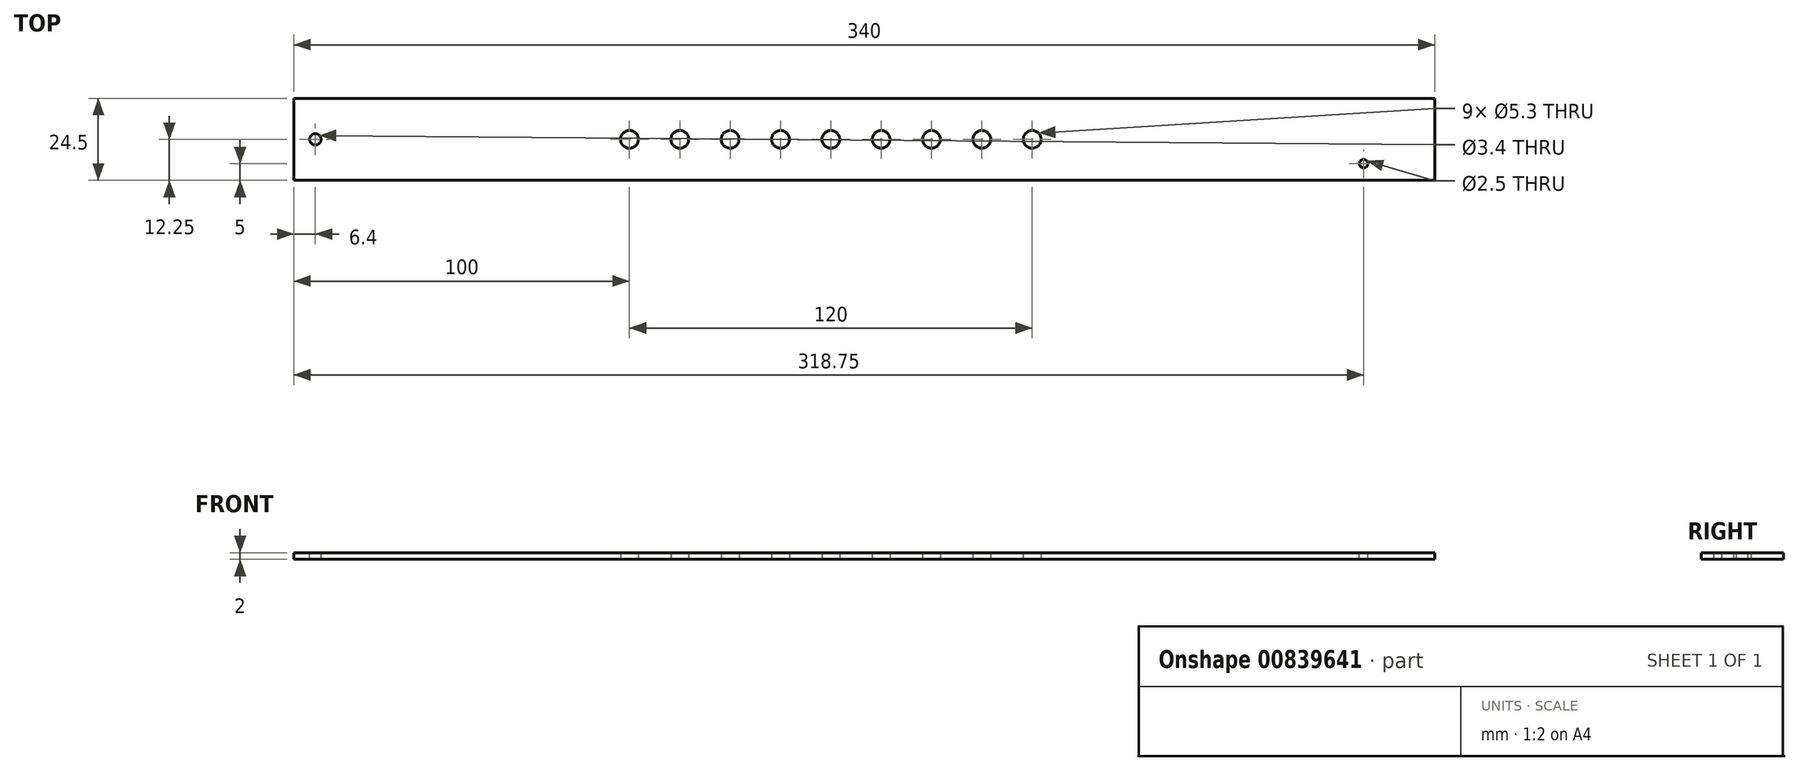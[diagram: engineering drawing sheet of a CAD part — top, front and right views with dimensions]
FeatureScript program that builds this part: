
annotation { "Feature Type Name" : "Feature", "Feature Type Description" : "" }
export const myFeature = defineFeature(function(context is Context, id is Id, definition is map)
    precondition{}
    {
        {
            var Q0;
            Q0=qCreatedBy(makeId("Top.planeOp"),FACE);
            var sketch = newSketch(context, id + "F0", { "sketchPlane" : qUnion([Q0])});
            skLineSegment(sketch, "E0.bottom", {"start": v(150, -12.25) * mm, "end": v(-150, -12.25) * mm});
            skLineSegment(sketch, "E0.top", {"start": v(150, 12.25) * mm, "end": v(-150, 12.25) * mm});
            skLineSegment(sketch, "E0.left", {"start": v(150, -12.25) * mm, "end": v(150, 12.25) * mm});
            skLineSegment(sketch, "E0.right", {"start": v(-150, -12.25) * mm, "end": v(-150, 12.25) * mm});
            skPoint(sketch, "E0.middle", {"position": v(0, 0) * mm});
            skCircle(sketch, "E1.5.0.0", {"center": v(-60, 0) * mm, "radius": 2.65 * mm});
            skCircle(sketch, "E1.6.0.0", {"center": v(-45, 0) * mm, "radius": 2.65 * mm});
            skCircle(sketch, "E1.7.0.0", {"center": v(-30, 0) * mm, "radius": 2.65 * mm});
            skCircle(sketch, "E1.8.0.0", {"center": v(-15, 0) * mm, "radius": 2.65 * mm});
            skCircle(sketch, "E1.9.0.0", {"center": v(0, 0) * mm, "radius": 2.65 * mm});
            skCircle(sketch, "E1.10.0.0", {"center": v(15, 0) * mm, "radius": 2.65 * mm});
            skCircle(sketch, "E1.11.0.0", {"center": v(30, 0) * mm, "radius": 2.65 * mm});
            skCircle(sketch, "E1.12.0.0", {"center": v(45, 0) * mm, "radius": 2.65 * mm});
            skCircle(sketch, "E1.13.0.0", {"center": v(60, 0) * mm, "radius": 2.65 * mm});
            skLineSegment(sketch, "E1.direction1", {"start": v(-135, 0) * mm, "end": v(-120, 0) * mm, "construction": true});
            skSolve(sketch);
        }
        {
            var Q0;
            Q0=makeQuery(id+"F0.imprint","IMPRINT",FACE,{"disambiguationData":[TD([[makeQuery(id+"F0.imprint","IMPRINT",EDGE,{"derivedFrom":sQuery(id+"F0.wireOp",EDGE,"E0.bottom")}),-1.0]])]});
            extrude(context, id + "F1", {"entities" : qUnion([Q0]), "depth" : 2 * mm, "offsetDistance" : 25 * mm});
        }
        {
            var Q0;
            Q0=makeQuery(id+"F1.opExtrude","SWEPT_FACE",FACE,{"disambiguationData":[OSD([sQuery(id+"F0.wireOp",EDGE,"E0.right")])]});
            extrude(context, id + "F2", {"entities" : qUnion([Q0]), "operationType" : NewBodyOperationType.ADD, "depth" : 10 * mm, "offsetDistance" : 25 * mm});
        }
        {
            var Q0;
            Q0=makeQuery(id+"F1.opExtrude","SWEPT_FACE",FACE,{"disambiguationData":[OSD([sQuery(id+"F0.wireOp",EDGE,"E0.left")])]});
            extrude(context, id + "F3", {"entities" : qUnion([Q0]), "operationType" : NewBodyOperationType.ADD, "depth" : 30 * mm, "offsetDistance" : 25 * mm});
        }
        {
            var Q0;
            {var subQ0=sQuery(id+"F0.wireOp",EDGE,"E0.left");var subQ1=sQuery(id+"F0.wireOp",EDGE,"E0.right");Q0=makeQuery(id+"F3.boolean.opBoolean","MERGE",FACE,{"derivedFrom":[makeQuery(id+"F2.boolean.opBoolean","MERGE",FACE,{"derivedFrom":[makeQuery(id+"F1.opExtrude","CAP_FACE",FACE,{"disambiguationData":[OSD([sQuery(id+"F0.wireOp",EDGE,"E0.bottom"),sQuery(id+"F0.wireOp",EDGE,"E0.top"),subQ0,subQ1,sQuery(id+"F0.wireOp",EDGE,"LckrCdrf-Oz9b-iWqB-HkfW-gHpTPrbceAxr"),sQuery(id+"F0.wireOp",EDGE,"E1.1.0.0"),sQuery(id+"F0.wireOp",EDGE,"E1.2.0.0"),sQuery(id+"F0.wireOp",EDGE,"E1.3.0.0"),sQuery(id+"F0.wireOp",EDGE,"E1.4.0.0"),sQuery(id+"F0.wireOp",EDGE,"E1.5.0.0"),sQuery(id+"F0.wireOp",EDGE,"E1.6.0.0"),sQuery(id+"F0.wireOp",EDGE,"E1.7.0.0"),sQuery(id+"F0.wireOp",EDGE,"E1.8.0.0"),sQuery(id+"F0.wireOp",EDGE,"E1.9.0.0"),sQuery(id+"F0.wireOp",EDGE,"E1.10.0.0"),sQuery(id+"F0.wireOp",EDGE,"E1.11.0.0"),sQuery(id+"F0.wireOp",EDGE,"E1.12.0.0"),sQuery(id+"F0.wireOp",EDGE,"E1.13.0.0"),sQuery(id+"F0.wireOp",EDGE,"E1.14.0.0"),sQuery(id+"F0.wireOp",EDGE,"E1.15.0.0"),sQuery(id+"F0.wireOp",EDGE,"E1.16.0.0"),sQuery(id+"F0.wireOp",EDGE,"E1.17.0.0"),sQuery(id+"F0.wireOp",EDGE,"E1.18.0.0")])],"isStart":false}),makeQuery(id+"F2.opExtrude","SWEPT_FACE",FACE,{"disambiguationData":[OSD([subQ1]),TDD([makeQuery(id+"F1.opExtrude","CAP_EDGE",EDGE,{"disambiguationData":[OSD([subQ1])],"isStart":false})])]})]}),makeQuery(id+"F3.opExtrude","SWEPT_FACE",FACE,{"disambiguationData":[OSD([subQ0]),TDD([makeQuery(id+"F1.opExtrude","CAP_EDGE",EDGE,{"disambiguationData":[OSD([subQ0])],"isStart":false})])]})]});}
            var sketch = newSketch(context, id + "F4", { "sketchPlane" : qUnion([Q0])});
            skCircle(sketch, "E2", {"center": v(-153.6, 0) * mm, "radius": 1.7 * mm});
            skSolve(sketch);
        }
        {
            var Q0;
            Q0=makeQuery(id+"F4.imprint","IMPRINT",FACE,{"disambiguationData":[TD([[makeQuery(id+"F4.imprint","IMPRINT",EDGE,{"derivedFrom":sQuery(id+"F4.wireOp",EDGE,"E2")}),1.0]])]});
            extrude(context, id + "F5", {"entities" : qUnion([Q0]), "operationType" : NewBodyOperationType.REMOVE, "endBound" : BoundingType.UP_TO_NEXT, "oppositeDirection" : true, "depth" : 25 * mm, "offsetDistance" : 25 * mm});
        }
        {
            var Q0;
            {var subQ0=sQuery(id+"F0.wireOp",EDGE,"E0.left");var subQ1=sQuery(id+"F0.wireOp",EDGE,"E0.right");Q0=makeQuery(id+"F3.boolean.opBoolean","MERGE",FACE,{"derivedFrom":[makeQuery(id+"F2.boolean.opBoolean","MERGE",FACE,{"derivedFrom":[makeQuery(id+"F1.opExtrude","CAP_FACE",FACE,{"disambiguationData":[OSD([sQuery(id+"F0.wireOp",EDGE,"E0.bottom"),sQuery(id+"F0.wireOp",EDGE,"E0.top"),subQ0,subQ1,sQuery(id+"F0.wireOp",EDGE,"LckrCdrf-Oz9b-iWqB-HkfW-gHpTPrbceAxr"),sQuery(id+"F0.wireOp",EDGE,"E1.1.0.0"),sQuery(id+"F0.wireOp",EDGE,"E1.2.0.0"),sQuery(id+"F0.wireOp",EDGE,"E1.3.0.0"),sQuery(id+"F0.wireOp",EDGE,"E1.4.0.0"),sQuery(id+"F0.wireOp",EDGE,"E1.5.0.0"),sQuery(id+"F0.wireOp",EDGE,"E1.6.0.0"),sQuery(id+"F0.wireOp",EDGE,"E1.7.0.0"),sQuery(id+"F0.wireOp",EDGE,"E1.8.0.0"),sQuery(id+"F0.wireOp",EDGE,"E1.9.0.0"),sQuery(id+"F0.wireOp",EDGE,"E1.10.0.0"),sQuery(id+"F0.wireOp",EDGE,"E1.11.0.0"),sQuery(id+"F0.wireOp",EDGE,"E1.12.0.0"),sQuery(id+"F0.wireOp",EDGE,"E1.13.0.0"),sQuery(id+"F0.wireOp",EDGE,"E1.14.0.0"),sQuery(id+"F0.wireOp",EDGE,"E1.15.0.0"),sQuery(id+"F0.wireOp",EDGE,"E1.16.0.0"),sQuery(id+"F0.wireOp",EDGE,"E1.17.0.0"),sQuery(id+"F0.wireOp",EDGE,"E1.18.0.0")])],"isStart":false}),makeQuery(id+"F2.opExtrude","SWEPT_FACE",FACE,{"disambiguationData":[OSD([subQ1]),TDD([makeQuery(id+"F1.opExtrude","CAP_EDGE",EDGE,{"disambiguationData":[OSD([subQ1])],"isStart":false})])]})]}),makeQuery(id+"F3.opExtrude","SWEPT_FACE",FACE,{"disambiguationData":[OSD([subQ0]),TDD([makeQuery(id+"F1.opExtrude","CAP_EDGE",EDGE,{"disambiguationData":[OSD([subQ0])],"isStart":false})])]})]});}
            var sketch = newSketch(context, id + "F6", { "sketchPlane" : qUnion([Q0])});
            skCircle(sketch, "E3", {"center": v(158.75, -7.25) * mm, "radius": 1.25 * mm});
            skSolve(sketch);
        }
        {
            var Q0;
            Q0=makeQuery(id+"F6.imprint","IMPRINT",FACE,{"disambiguationData":[TD([[makeQuery(id+"F6.imprint","IMPRINT",EDGE,{"derivedFrom":sQuery(id+"F6.wireOp",EDGE,"E3")}),1.0]])]});
            extrude(context, id + "F7", {"entities" : qUnion([Q0]), "operationType" : NewBodyOperationType.REMOVE, "endBound" : BoundingType.UP_TO_NEXT, "oppositeDirection" : true, "depth" : 25 * mm, "offsetDistance" : 25 * mm});
        }
    });
